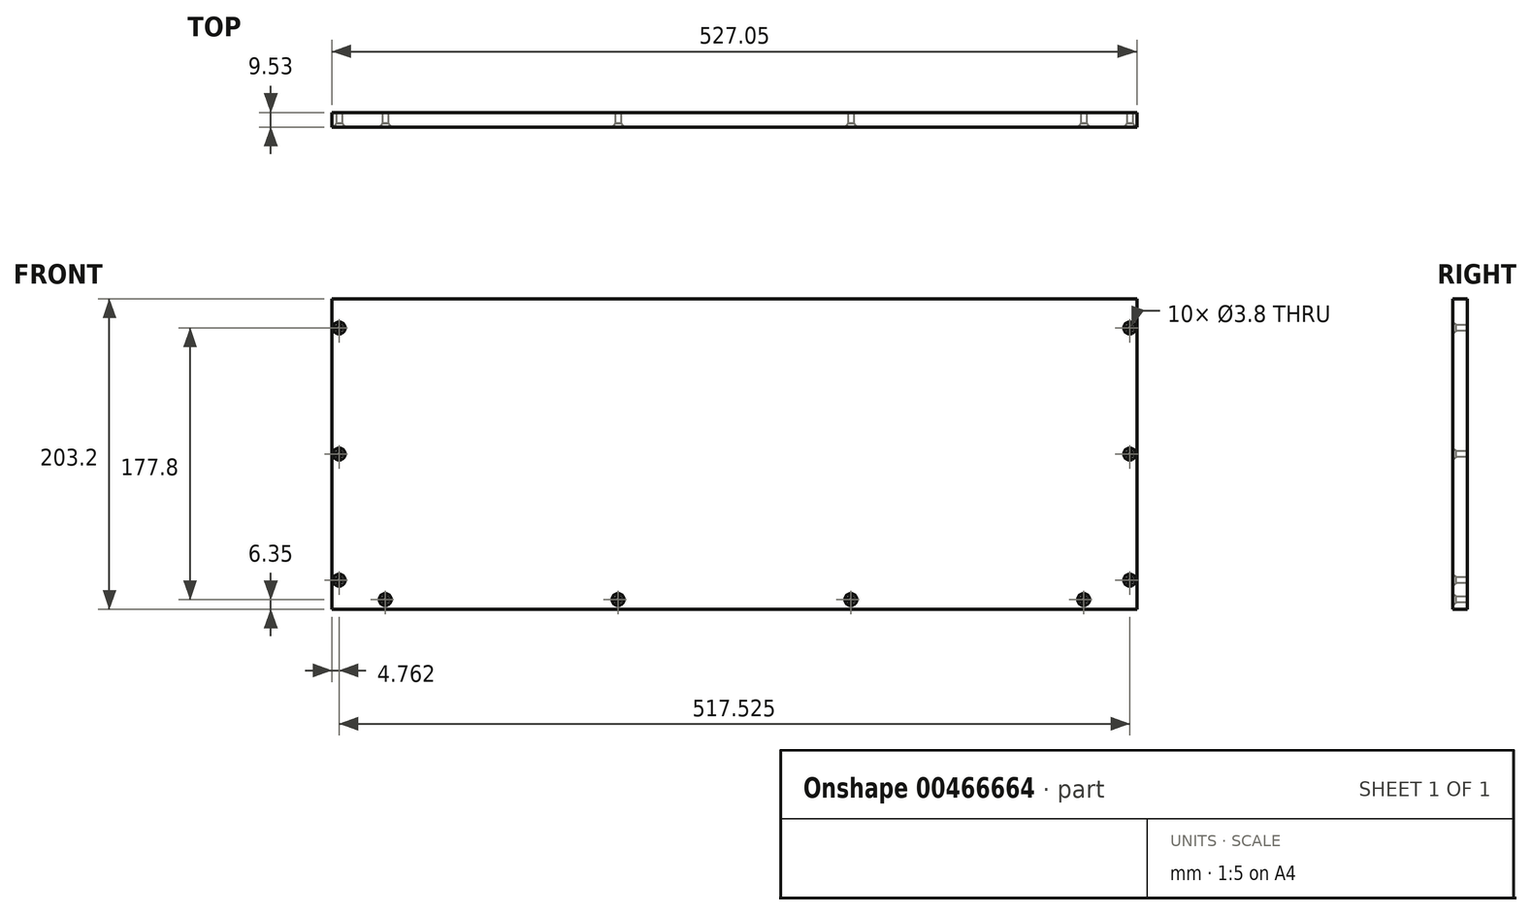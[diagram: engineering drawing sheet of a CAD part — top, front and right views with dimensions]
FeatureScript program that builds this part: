
annotation { "Feature Type Name" : "Feature", "Feature Type Description" : "" }
export const myFeature = defineFeature(function(context is Context, id is Id, definition is map)
    precondition{}
    {
        {
            var Q0;
            Q0=qCreatedBy(makeId("Front.planeOp"),FACE);
            var sketch = newSketch(context, id + "F0", { "sketchPlane" : qUnion([Q0])});
            skLineSegment(sketch, "E0.bottom", {"start": v(0, 0) * mm, "end": v(-527.05, 0) * mm});
            skLineSegment(sketch, "E0.top", {"start": v(0, 203.2) * mm, "end": v(-527.05, 203.2) * mm});
            skLineSegment(sketch, "E0.left", {"start": v(0, 0) * mm, "end": v(0, 203.2) * mm});
            skLineSegment(sketch, "E0.right", {"start": v(-527.05, 0) * mm, "end": v(-527.05, 203.2) * mm});
            skSolve(sketch);
        }
        {
            var Q0;
            Q0=makeQuery(id+"F0.imprint","IMPRINT",FACE,{"disambiguationData":[TD([[makeQuery(id+"F0.imprint","IMPRINT",EDGE,{"derivedFrom":sQuery(id+"F0.wireOp",EDGE,"E0.bottom")}),-1.0]])]});
            extrude(context, id + "F1", {"entities" : qUnion([Q0]), "depth" : 9.52 * mm});
        }
        {
            var Q0;
            Q0=makeQuery(id+"F1.opExtrude","CAP_FACE",FACE,{"disambiguationData":[OSD([sQuery(id+"F0.wireOp",EDGE,"E0.bottom"),sQuery(id+"F0.wireOp",EDGE,"E0.top"),sQuery(id+"F0.wireOp",EDGE,"E0.left"),sQuery(id+"F0.wireOp",EDGE,"E0.right")])],"isStart":false});
            var sketch = newSketch(context, id + "F2", { "sketchPlane" : qUnion([Q0])});
            skPoint(sketch, "E1", {"position": v(-492.13, 6.35) * mm});
            skPoint(sketch, "E2", {"position": v(-522.29, 19.05) * mm});
            skPoint(sketch, "E3", {"position": v(-4.76, 19.05) * mm});
            skPoint(sketch, "E4.1.0.0", {"position": v(-339.73, 6.35) * mm});
            skPoint(sketch, "E4.2.0.0", {"position": v(-187.33, 6.35) * mm});
            skPoint(sketch, "E4.3.0.0", {"position": v(-34.93, 6.35) * mm});
            skLineSegment(sketch, "E4.direction1", {"start": v(-501.65, 6.35) * mm, "end": v(-349.25, 6.35) * mm, "construction": true});
            skPoint(sketch, "E5.0.1.0", {"position": v(-522.29, 101.6) * mm});
            skPoint(sketch, "E5.0.2.0", {"position": v(-522.29, 184.15) * mm});
            skLineSegment(sketch, "E5.direction1", {"start": v(-522.29, 19.05) * mm, "end": v(-496.89, 19.05) * mm, "construction": true});
            skLineSegment(sketch, "E5.direction2", {"start": v(-522.29, 19.05) * mm, "end": v(-522.29, 101.6) * mm, "construction": true});
            skPoint(sketch, "E6.0.1.0", {"position": v(-4.76, 101.6) * mm});
            skPoint(sketch, "E6.0.2.0", {"position": v(-4.76, 184.15) * mm});
            skLineSegment(sketch, "E6.direction1", {"start": v(-4.76, 19.05) * mm, "end": v(20.64, 19.05) * mm, "construction": true});
            skLineSegment(sketch, "E6.direction2", {"start": v(-4.76, 19.05) * mm, "end": v(-4.76, 101.6) * mm, "construction": true});
            skSolve(sketch);
        }
        {
            var Q0;
            Q0=sQuery(id+"F2.wireOp",VERTEX,"E6.0.2.0");
            var Q1;
            Q1=sQuery(id+"F2.wireOp",VERTEX,"E6.0.1.0");
            var Q2;
            Q2=sQuery(id+"F2.wireOp",VERTEX,"E3");
            var Q3;
            Q3=sQuery(id+"F2.wireOp",VERTEX,"E4.3.0.0");
            var Q4;
            Q4=sQuery(id+"F2.wireOp",VERTEX,"E4.2.0.0");
            var Q5;
            Q5=sQuery(id+"F2.wireOp",VERTEX,"E4.1.0.0");
            var Q6;
            Q6=sQuery(id+"F2.wireOp",VERTEX,"E1");
            var Q7;
            Q7=sQuery(id+"F2.wireOp",VERTEX,"E2");
            var Q8;
            Q8=sQuery(id+"F2.wireOp",VERTEX,"E5.0.1.0");
            var Q9;
            Q9=sQuery(id+"F2.wireOp",VERTEX,"E5.0.2.0");
            var Q10;
            Q10=makeQuery(id+"F1.opExtrude","SWEPT_BODY",BODY,{"disambiguationData":[OSD([sQuery(id+"F0.wireOp",EDGE,"E0.bottom"),sQuery(id+"F0.wireOp",EDGE,"E0.top"),sQuery(id+"F0.wireOp",EDGE,"E0.left"),sQuery(id+"F0.wireOp",EDGE,"E0.right")])]});
            hole(context, id + "F3", {"style" : HoleStyle.C_SINK, "endStyle" : HoleEndStyle.BLIND, "standardTappedOrClearance" : lookupTablePath({ "standard" : "ANSI", "fit" : "Normal (ASME)", "size" : "#6", "type" : "Clearance" }), "standardBlindInLast" : lookupTablePath({ "fit" : "Free", "standard" : "ANSI", "size" : "#6", "type" : "Clearance" }), "holeDiameter" : 3.8 * mm, "cSinkDiameter" : 7.8 * mm, "cSinkAngle" : 82 * degree, "holeDepth" : 13.5 * mm, "isTappedThrough" : true, "tappedDepth" : 9.52 * mm, "tapClearance" : 5, "locations" : qUnion([Q0, Q1, Q2, Q3, Q4, Q5, Q6, Q7, Q8, Q9]), "scope" : qUnion([Q10])});
        }
    });
